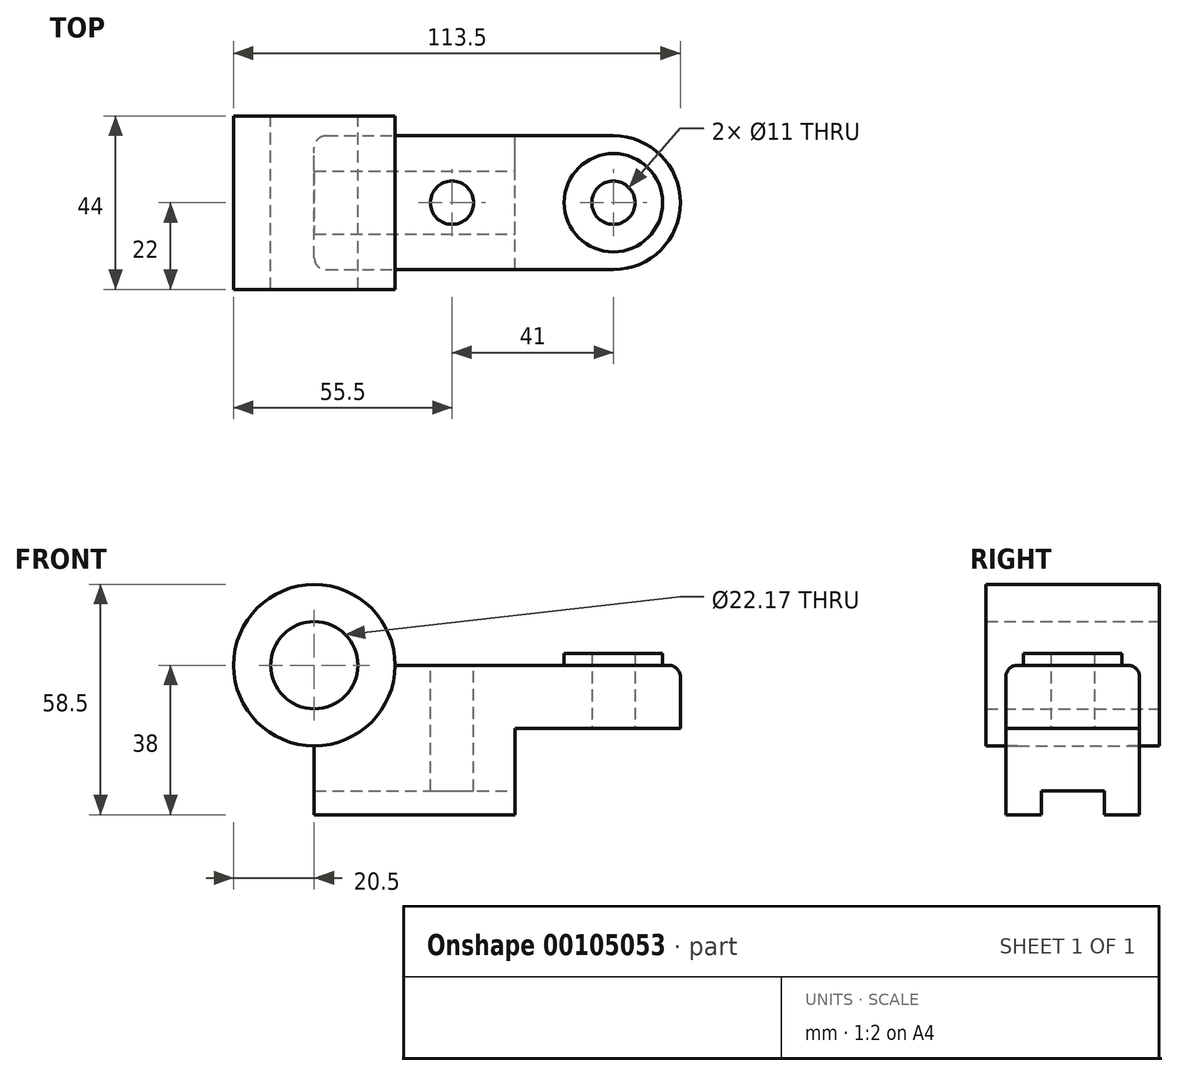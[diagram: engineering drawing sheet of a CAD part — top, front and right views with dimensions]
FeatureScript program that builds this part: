
annotation { "Feature Type Name" : "Feature", "Feature Type Description" : "" }
export const myFeature = defineFeature(function(context is Context, id is Id, definition is map)
    precondition{}
    {
        {
            var Q0;
            Q0=qCreatedBy(makeId("Front.planeOp"),FACE);
            var sketch = newSketch(context, id + "F0", { "sketchPlane" : qUnion([Q0])});
            skLineSegment(sketch, "E0.top", {"start": v(0, 38) * mm, "end": v(76, 38) * mm});
            skLineSegment(sketch, "E0.left", {"start": v(0, 0) * mm, "end": v(0, 38) * mm});
            skCircle(sketch, "E1", {"center": v(0, 38) * mm, "radius": 11.09 * mm});
            skCircle(sketch, "E2", {"center": v(0, 38) * mm, "radius": 20.5 * mm});
            skLineSegment(sketch, "E3", {"start": v(0, 0) * mm, "end": v(51, 0) * mm});
            skLineSegment(sketch, "E4", {"start": v(51, 0) * mm, "end": v(51, 22) * mm});
            skLineSegment(sketch, "E5", {"start": v(51, 22) * mm, "end": v(76, 22) * mm});
            skLineSegment(sketch, "E6", {"start": v(76, 22) * mm, "end": v(76, 38) * mm});
            skSolve(sketch);
        }
        {
            var Q0;
            {var subQ0=sQuery(id+"F0.wireOp",EDGE,"E3");Q0=makeQuery(id+"F0.imprint","IMPRINT",FACE,{"disambiguationData":[TD([[makeQuery(id+"F0.imprint","IMPRINT",EDGE,{"derivedFrom":subQ0}),1.0]])]});}
            extrude(context, id + "F1", {"entities" : qUnion([Q0]), "endBound" : BoundingType.SYMMETRIC, "depth" : 17 * 2 * mm});
        }
        {
            var Q0;
            {var subQ0=sQuery(id+"F0.wireOp",EDGE,"E2");var subQ1=sQuery(id+"F0.wireOp",EDGE,"E0.top");var subQ2=makeQuery(id+"F0.imprint","INTERSECT",VERTEX,{"derivedFrom":[subQ1,subQ0]});Q0=makeQuery(id+"F0.imprint","IMPRINT",FACE,{"disambiguationData":[TD([[makeQuery(id+"F0.imprint","IMPRINT",EDGE,{"disambiguationData":[TD([[subQ2,1.0]])],"derivedFrom":subQ1}),1.0]])]});}
            var Q1;
            {var subQ0=sQuery(id+"F0.wireOp",EDGE,"E2");var subQ1=sQuery(id+"F0.wireOp",EDGE,"E0.top");var subQ2=makeQuery(id+"F0.imprint","INTERSECT",VERTEX,{"derivedFrom":[subQ1,subQ0]});Q1=makeQuery(id+"F0.imprint","IMPRINT",FACE,{"disambiguationData":[TD([[makeQuery(id+"F0.imprint","IMPRINT",EDGE,{"disambiguationData":[TD([[subQ2,1.0]])],"derivedFrom":subQ1}),-1.0]])]});}
            extrude(context, id + "F2", {"entities" : qUnion([Q0, Q1]), "operationType" : NewBodyOperationType.ADD, "endBound" : BoundingType.SYMMETRIC, "depth" : 44 * mm});
        }
        {
            var Q0;
            Q0=makeQuery(id+"F1.opExtrude","SWEPT_FACE",FACE,{"disambiguationData":[OSD([sQuery(id+"F0.wireOp",EDGE,"E0.top")])]});
            var sketch = newSketch(context, id + "F3", { "sketchPlane" : qUnion([Q0])});
            skArc(sketch, "E7", {"start": v(76, -17) * mm, "mid": v(93, 0) * mm, "end": v(76, 17) * mm});
            skCircle(sketch, "E8", {"center": v(35, 0) * mm, "radius": 5.5 * mm});
            skSolve(sketch);
        }
        {
            var Q0;
            Q0=makeQuery(id+"F3.imprint","IMPRINT",FACE,{"disambiguationData":[TD([[makeQuery(id+"F3.imprint","IMPRINT",EDGE,{"derivedFrom":sQuery(id+"F3.wireOp",EDGE,"E7")}),1.0]])]});
            var Q1;
            Q1=makeQuery(id+"F1.opExtrude","SWEPT_FACE",FACE,{"disambiguationData":[OSD([sQuery(id+"F0.wireOp",EDGE,"E5")])]});
            extrude(context, id + "F4", {"entities" : qUnion([Q0]), "operationType" : NewBodyOperationType.ADD, "endBound" : BoundingType.UP_TO_SURFACE, "oppositeDirection" : true, "endBoundEntityFace" : qUnion([Q1]), "depth" : 25 * mm});
        }
        {
            var Q0;
            {var subQ0=sQuery(id+"F0.wireOp",EDGE,"E0.top");Q0=makeQuery(id+"F4.boolean.opBoolean","MERGE",FACE,{"derivedFrom":[makeQuery(id+"F1.opExtrude","SWEPT_FACE",FACE,{"disambiguationData":[OSD([subQ0])]}),makeQuery(id+"F4.opExtrude","CAP_FACE",FACE,{"disambiguationData":[OSD([subQ0,sQuery(id+"F0.wireOp",EDGE,"E6"),sQuery(id+"F3.wireOp",EDGE,"E7")])],"isStart":true})]});}
            var sketch = newSketch(context, id + "F5", { "sketchPlane" : qUnion([Q0])});
            skCircle(sketch, "E9", {"center": v(76, 0) * mm, "radius": 12.5 * mm});
            skCircle(sketch, "E10", {"center": v(35, 0) * mm, "radius": 5.5 * mm});
            skCircle(sketch, "E11", {"center": v(76, 0) * mm, "radius": 5.5 * mm});
            skSolve(sketch);
        }
        {
            var Q0;
            Q0=makeQuery(id+"F5.imprint","IMPRINT",FACE,{"disambiguationData":[TD([[makeQuery(id+"F5.imprint","IMPRINT",EDGE,{"derivedFrom":sQuery(id+"F5.wireOp",EDGE,"E9")}),1.0]])]});
            extrude(context, id + "F6", {"entities" : qUnion([Q0]), "operationType" : NewBodyOperationType.ADD, "depth" : 3 * mm});
        }
        {
            var Q0;
            Q0=makeQuery(id+"F5.imprint","IMPRINT",FACE,{"disambiguationData":[TD([[makeQuery(id+"F5.imprint","IMPRINT",EDGE,{"derivedFrom":sQuery(id+"F5.wireOp",EDGE,"E10")}),1.0]])]});
            extrude(context, id + "F7", {"entities" : qUnion([Q0]), "operationType" : NewBodyOperationType.REMOVE, "endBound" : BoundingType.THROUGH_ALL, "oppositeDirection" : true, "depth" : 25 * mm});
        }
        {
            var Q0;
            Q0=makeQuery(id+"F5.imprint","IMPRINT",FACE,{"disambiguationData":[TD([[makeQuery(id+"F5.imprint","IMPRINT",EDGE,{"derivedFrom":sQuery(id+"F5.wireOp",EDGE,"E11")}),1.0]])]});
            extrude(context, id + "F8", {"entities" : qUnion([Q0]), "operationType" : NewBodyOperationType.REMOVE, "endBound" : BoundingType.THROUGH_ALL, "oppositeDirection" : true, "depth" : 25 * mm});
        }
        {
            var Q0;
            Q0=makeQuery(id+"F1.opExtrude","SWEPT_FACE",FACE,{"disambiguationData":[OSD([sQuery(id+"F0.wireOp",EDGE,"E4")])]});
            var sketch = newSketch(context, id + "F9", { "sketchPlane" : qUnion([Q0])});
            skLineSegment(sketch, "E12.bottom", {"start": v(-8, 0) * mm, "end": v(8, 0) * mm});
            skLineSegment(sketch, "E12.top", {"start": v(-8, 6) * mm, "end": v(8, 6) * mm});
            skLineSegment(sketch, "E12.left", {"start": v(-8, 0) * mm, "end": v(-8, 6) * mm});
            skLineSegment(sketch, "E12.right", {"start": v(8, 0) * mm, "end": v(8, 6) * mm});
            skSolve(sketch);
        }
        {
            var Q0;
            Q0=makeQuery(id+"F9.imprint","IMPRINT",FACE,{"disambiguationData":[TD([[makeQuery(id+"F9.imprint","IMPRINT",EDGE,{"derivedFrom":sQuery(id+"F9.wireOp",EDGE,"E12.bottom")}),1.0]])]});
            extrude(context, id + "F10", {"entities" : qUnion([Q0]), "operationType" : NewBodyOperationType.REMOVE, "endBound" : BoundingType.THROUGH_ALL, "oppositeDirection" : true, "depth" : 25 * mm});
        }
        {
            var Q0;
            Q0=makeQuery(id+"F1.opExtrude","SWEPT_EDGE",EDGE,{"disambiguationData":[OSD([sQuery(id+"F0.wireOp",EDGE,"E0.top"),sQuery(id+"F0.wireOp",EDGE,"E2")])]});
            var Q1;
            Q1=makeQuery(id+"F6.opExtrude","CAP_EDGE",EDGE,{"disambiguationData":[OSD([sQuery(id+"F5.wireOp",EDGE,"E9")])],"isStart":true});
            var Q2;
            Q2=makeQuery(id+"F1.opExtrude","CAP_EDGE",EDGE,{"disambiguationData":[OSD([sQuery(id+"F0.wireOp",EDGE,"E2")])],"isStart":false});
            var Q3;
            Q3=makeQuery(id+"F1.opExtrude","CAP_EDGE",EDGE,{"disambiguationData":[OSD([sQuery(id+"F0.wireOp",EDGE,"E0.left")])],"isStart":false});
            var Q4;
            Q4=makeQuery(id+"F1.opExtrude","CAP_EDGE",EDGE,{"disambiguationData":[OSD([sQuery(id+"F0.wireOp",EDGE,"E2")])],"isStart":true});
            var Q5;
            Q5=makeQuery(id+"F1.opExtrude","CAP_EDGE",EDGE,{"disambiguationData":[OSD([sQuery(id+"F0.wireOp",EDGE,"E0.left")])],"isStart":true});
            fillet(context, id + "F11", {"entities" : qUnion([Q0, Q1, Q2, Q3, Q4, Q5]), "radius" : 3 * mm, "tangentPropagation" : true, "allowEdgeOverflow" : false});
        }
        {
            var Q0;
            Q0=makeQuery(id+"F1.opExtrude","CAP_EDGE",EDGE,{"disambiguationData":[OSD([sQuery(id+"F0.wireOp",EDGE,"E0.top")])],"isStart":false});
            var Q1;
            Q1=makeQuery(id+"F11.opFillet","BLEND_EDGE",EDGE,{"blendedFrom":[makeQuery(id+"F6.opExtrude","CAP_EDGE",EDGE,{"disambiguationData":[OSD([sQuery(id+"F5.wireOp",EDGE,"E9")])],"isStart":true}),makeQuery(id+"F4.opExtrude","SWEPT_FACE",FACE,{"disambiguationData":[OSD([sQuery(id+"F3.wireOp",EDGE,"E7")])]})],"blendedInto":[makeQuery(id+"F4.opExtrude","SWEPT_FACE",FACE,{"disambiguationData":[OSD([sQuery(id+"F3.wireOp",EDGE,"E7")])]})]});
            fillet(context, id + "F12", {"entities" : qUnion([Q0, Q1]), "radius" : 3 * mm, "tangentPropagation" : true, "allowEdgeOverflow" : false});
        }
    });
